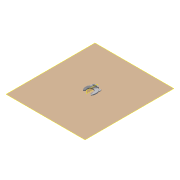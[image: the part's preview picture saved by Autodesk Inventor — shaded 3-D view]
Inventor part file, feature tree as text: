
AUTODESK INVENTOR PART (.ipt)
format: ipt  version: 2014 (Build 180170000, 170)  size: 464,896 bytes
history: native  units: mm
features: fillet x8, extrude x4, sketch x4, plane x2
ambient origin geometry x8: Origin, YZ Plane, XZ Plane, XY Plane, X Axis, Y Axis, Z Axis, Center Point
bodies: Solid1 (feature_tree)
feature tree (18):
  plane  "Work Plane1"
  plane  "Work Plane2"
  extrude  "Extrusion1"  Depth=0.5mm
  fillet  "Fillet1"  Radius=0.5mm
  fillet  "Fillet2"  Radius=5.5mm
  extrude  "Extrusion2"  Depth=8.726646mm
  fillet  "Fillet3"  Radius=1.0mm
  fillet  "Fillet4"  Radius=1.4mm
  extrude  "Extrusion3"  Depth=22.68928mm
  fillet  "Fillet5"  Radius=10.7mm
  fillet  "Fillet6"  Radius=1.5mm
  extrude  "Extrusion4"  Depth=0.3mm
  fillet  "Fillet7"  Radius=1.745329mm
  fillet  "Fillet8"  Radius=15.0mm
  sketch  "Sketch2"  dims[d3=6.15mm d4=0.5mm d5=0.5mm d6=5.5mm]
  sketch  "Sketch3"  dims[d7=8.726646mm d8=8.726646mm d9=1.0mm d10=-0.349066mm d11=1.4mm]
  sketch  "Sketch4"  dims[d12=0.5mm d14=22.68928mm d15=22.68928mm d16=10.7mm d17=1.5mm d18=-0.349066mm]
  sketch  "Sketch5"  dims[d19=0.3mm d20=0.5mm d21=1.745329mm d22=15.0mm d23=0.0mm d24=7.0mm d25=0.2mm d26=5.35mm d27=24.43461mm d28=22.68928mm d29=22.68928mm d30=0.5mm d31=24.43461mm d32=0.5mm d33=3.0mm d34=3.0mm d35=0.6mm d36=-0.349066mm d37=0.2mm d38=0.3mm]
